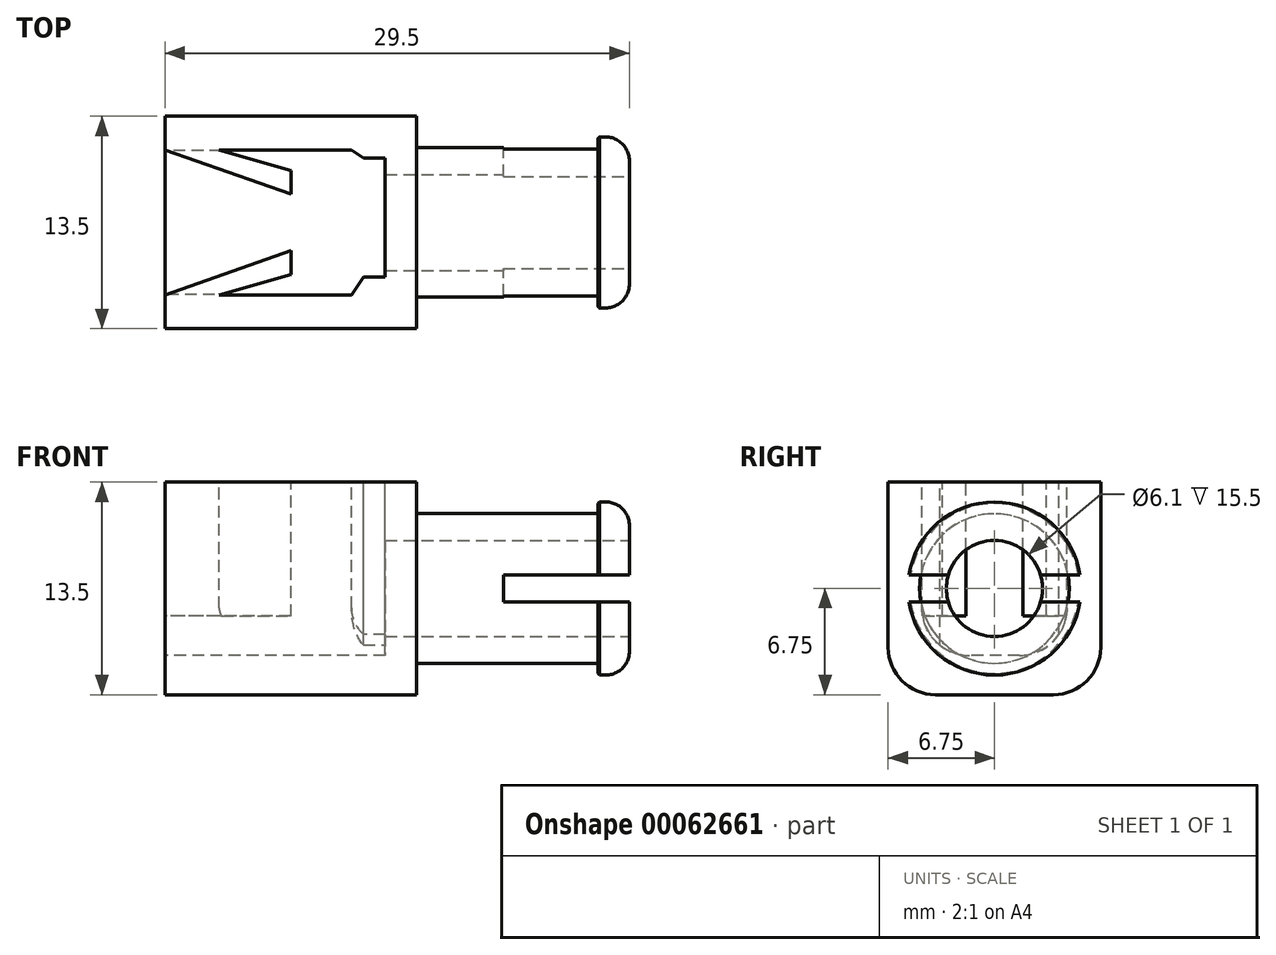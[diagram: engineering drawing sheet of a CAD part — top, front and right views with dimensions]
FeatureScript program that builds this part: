
annotation { "Feature Type Name" : "Feature", "Feature Type Description" : "" }
export const myFeature = defineFeature(function(context is Context, id is Id, definition is map)
    precondition{}
    {
        {
            var Q0;
            Q0=qCreatedBy(makeId("Top.planeOp"),FACE);
            var sketch = newSketch(context, id + "F0", { "sketchPlane" : qUnion([Q0])});
            skLineSegment(sketch, "E0.rect.bottom", {"start": v(-8, 6.75) * mm, "end": v(8, 6.75) * mm});
            skLineSegment(sketch, "E0.rect.top", {"start": v(-8, -6.75) * mm, "end": v(8, -6.75) * mm});
            skLineSegment(sketch, "E0.rect.left", {"start": v(-8, 6.75) * mm, "end": v(-8, -6.75) * mm});
            skLineSegment(sketch, "E0.rect.right", {"start": v(8, 6.75) * mm, "end": v(8, -6.75) * mm});
            skPoint(sketch, "E0.rect.middle", {"position": v(0, 0) * mm});
            skSolve(sketch);
        }
        {
            var Q0;
            Q0 = qSketchRegion(id + "F0", true);
            extrude(context, id + "F1", {"entities" : qUnion([Q0]), "depth" : 13.5 * mm});
        }
        {
            var Q0;
            Q0=makeQuery(id+"F1.opExtrude","SWEPT_FACE",FACE,{"disambiguationData":[OSD([sQuery(id+"F0.wireOp",EDGE,"E0.rect.right")])]});
            var sketch = newSketch(context, id + "F2", { "sketchPlane" : qUnion([Q0])});
            skCircle(sketch, "E1", {"center": v(0, 6.75) * mm, "radius": 4.75 * mm});
            skPoint(sketch, "E1.centerSnap0", {"position": v(-6.75, 6.75) * mm});
            skSolve(sketch);
        }
        {
            var Q0;
            Q0 = qSketchRegion(id + "F2", true);
            extrude(context, id + "F3", {"entities" : qUnion([Q0]), "operationType" : NewBodyOperationType.ADD, "depth" : 11.5 * mm});
        }
        {
            var Q0;
            Q0=makeQuery(id+"F3.opExtrude","CAP_FACE",FACE,{"disambiguationData":[OSD([sQuery(id+"F2.wireOp",EDGE,"E1")])],"isStart":false});
            var sketch = newSketch(context, id + "F4", { "sketchPlane" : qUnion([Q0])});
            skCircle(sketch, "E2", {"center": v(0, 6.75) * mm, "radius": 5.5 * mm});
            skSolve(sketch);
        }
        {
            var Q0;
            Q0 = qSketchRegion(id + "F4", true);
            extrude(context, id + "F5", {"entities" : qUnion([Q0]), "operationType" : NewBodyOperationType.ADD, "depth" : 2 * mm});
        }
        {
            var Q0;
            Q0=makeQuery(id+"F1.opExtrude","CAP_FACE",FACE,{"disambiguationData":[OSD([sQuery(id+"F0.wireOp",EDGE,"E0.rect.bottom"),sQuery(id+"F0.wireOp",EDGE,"E0.rect.top"),sQuery(id+"F0.wireOp",EDGE,"E0.rect.left"),sQuery(id+"F0.wireOp",EDGE,"E0.rect.right")])],"isStart":false});
            var sketch = newSketch(context, id + "F6", { "sketchPlane" : qUnion([Q0])});
            skLineSegment(sketch, "E3", {"start": v(0, 1.8) * mm, "end": v(0, 3.3) * mm});
            skLineSegment(sketch, "E4", {"start": v(0, 3.3) * mm, "end": v(-4.55, 4.6) * mm});
            skLineSegment(sketch, "E5", {"start": v(-4.55, 4.6) * mm, "end": v(3.85, 4.6) * mm});
            skLineSegment(sketch, "E6", {"start": v(3.85, 4.6) * mm, "end": v(4.6, 4.09) * mm});
            skLineSegment(sketch, "E7", {"start": v(4.6, 4.09) * mm, "end": v(6, 4.09) * mm});
            skLineSegment(sketch, "E8", {"start": v(6, 4.09) * mm, "end": v(6, -3.47) * mm});
            skLineSegment(sketch, "E9", {"start": v(6, -3.47) * mm, "end": v(4.6, -3.47) * mm});
            skLineSegment(sketch, "E10", {"start": v(4.6, -3.47) * mm, "end": v(3.85, -4.6) * mm});
            skLineSegment(sketch, "E11", {"start": v(3.85, -4.6) * mm, "end": v(-4.55, -4.6) * mm});
            skLineSegment(sketch, "E12", {"start": v(-4.55, -4.6) * mm, "end": v(0, -3.3) * mm});
            skLineSegment(sketch, "E13", {"start": v(0, -3.3) * mm, "end": v(0, -1.8) * mm});
            skLineSegment(sketch, "E14", {"start": v(0, -1.8) * mm, "end": v(-8, -4.6) * mm});
            skLineSegment(sketch, "E15", {"start": v(-8, 4.6) * mm, "end": v(0, 1.8) * mm});
            skSolve(sketch);
        }
        {
            var Q0;
            Q0=makeQuery(id+"F6.imprint","IMPRINT",FACE,{"disambiguationData":[TD([[makeQuery(id+"F6.imprint","IMPRINT",EDGE,{"derivedFrom":sQuery(id+"F6.wireOp",EDGE,"E3")}),-1.0]])]});
            extrude(context, id + "F7", {"entities" : qUnion([Q0]), "operationType" : NewBodyOperationType.REMOVE, "oppositeDirection" : true, "depth" : 11 * mm});
        }
        {
            var Q0;
            Q0=makeQuery(id+"F5.opExtrude","CAP_FACE",FACE,{"disambiguationData":[OSD([sQuery(id+"F4.wireOp",EDGE,"E2")])],"isStart":false});
            var sketch = newSketch(context, id + "F8", { "sketchPlane" : qUnion([Q0])});
            skCircle(sketch, "E16", {"center": v(0, 6.75) * mm, "radius": 3.05 * mm});
            skSolve(sketch);
        }
        {
            var Q0;
            Q0 = qSketchRegion(id + "F8", true);
            extrude(context, id + "F9", {"entities" : qUnion([Q0]), "operationType" : NewBodyOperationType.REMOVE, "oppositeDirection" : true, "depth" : 17 * mm});
        }
        {
            var Q0;
            Q0=makeQuery(id+"F1.opExtrude","SWEPT_FACE",FACE,{"disambiguationData":[OSD([sQuery(id+"F0.wireOp",EDGE,"E0.rect.left")])]});
            var sketch = newSketch(context, id + "F10", { "sketchPlane" : qUnion([Q0])});
            skLineSegment(sketch, "E17.bottom", {"start": v(-4.6, 2.5) * mm, "end": v(4.6, 2.5) * mm});
            skLineSegment(sketch, "E17.top", {"start": v(-4.6, 5) * mm, "end": v(4.6, 5) * mm});
            skLineSegment(sketch, "E17.left", {"start": v(-4.6, 2.5) * mm, "end": v(-4.6, 5) * mm});
            skLineSegment(sketch, "E17.right", {"start": v(4.6, 2.5) * mm, "end": v(4.6, 5) * mm});
            skSolve(sketch);
        }
        {
            var Q0;
            Q0 = qSketchRegion(id + "F10", true);
            extrude(context, id + "F11", {"entities" : qUnion([Q0]), "operationType" : NewBodyOperationType.REMOVE, "oppositeDirection" : true, "depth" : 10 * mm});
        }
        {
            var Q0;
            Q0=makeQuery(id+"F5.opExtrude","CAP_FACE",FACE,{"disambiguationData":[OSD([sQuery(id+"F4.wireOp",EDGE,"E2")])],"isStart":false});
            var sketch = newSketch(context, id + "F12", { "sketchPlane" : qUnion([Q0])});
            skLineSegment(sketch, "E18.rect.bottom", {"start": v(-6.07, 7.6) * mm, "end": v(6.07, 7.6) * mm});
            skLineSegment(sketch, "E18.rect.top", {"start": v(-6.07, 5.9) * mm, "end": v(6.07, 5.9) * mm});
            skLineSegment(sketch, "E18.rect.left", {"start": v(-6.07, 7.6) * mm, "end": v(-6.07, 5.9) * mm});
            skLineSegment(sketch, "E18.rect.right", {"start": v(6.07, 7.6) * mm, "end": v(6.07, 5.9) * mm});
            skPoint(sketch, "E18.rect.middle", {"position": v(0, 6.75) * mm});
            skSolve(sketch);
        }
        {
            var Q0;
            Q0 = qSketchRegion(id + "F12", true);
            extrude(context, id + "F13", {"entities" : qUnion([Q0]), "operationType" : NewBodyOperationType.REMOVE, "oppositeDirection" : true, "depth" : 8 * mm});
        }
        {
            var Q0;
            Q0=makeQuery(id+"F11.boolean.opBoolean","MERGE",EDGE,{"derivedFrom":[makeQuery(id+"F7.boolean.opBoolean","COPY",EDGE,{"derivedFrom":makeQuery(id+"F7.opExtrude","CAP_EDGE",EDGE,{"disambiguationData":[OSD([sQuery(id+"F6.wireOp",EDGE,"E5")])],"isStart":false})}),makeQuery(id+"F11.opExtrude","SWEPT_EDGE",EDGE,{"disambiguationData":[OSD([sQuery(id+"F10.wireOp",EDGE,"508b1908-c477-498a-9574-35cd2a2e4f79.bottom"),sQuery(id+"F10.wireOp",EDGE,"508b1908-c477-498a-9574-35cd2a2e4f79.left")])]})]});
            var Q1;
            Q1=makeQuery(id+"F11.boolean.opBoolean","MERGE",EDGE,{"derivedFrom":[makeQuery(id+"F7.boolean.opBoolean","COPY",EDGE,{"derivedFrom":makeQuery(id+"F7.opExtrude","CAP_EDGE",EDGE,{"disambiguationData":[OSD([sQuery(id+"F6.wireOp",EDGE,"E11")])],"isStart":false})}),makeQuery(id+"F11.opExtrude","SWEPT_EDGE",EDGE,{"disambiguationData":[OSD([sQuery(id+"F10.wireOp",EDGE,"508b1908-c477-498a-9574-35cd2a2e4f79.bottom"),sQuery(id+"F10.wireOp",EDGE,"508b1908-c477-498a-9574-35cd2a2e4f79.right")])]})]});
            var Q2;
            Q2=makeQuery(id+"F1.opExtrude","CAP_EDGE",EDGE,{"disambiguationData":[OSD([sQuery(id+"F0.wireOp",EDGE,"E0.rect.bottom")])],"isStart":true});
            var Q3;
            Q3=makeQuery(id+"F1.opExtrude","CAP_EDGE",EDGE,{"disambiguationData":[OSD([sQuery(id+"F0.wireOp",EDGE,"E0.rect.top")])],"isStart":true});
            var Q4;
            Q4=makeQuery(id+"F7.boolean.opBoolean","COPY",EDGE,{"derivedFrom":makeQuery(id+"F7.opExtrude","CAP_EDGE",EDGE,{"disambiguationData":[OSD([sQuery(id+"F6.wireOp",EDGE,"E11")])],"isStart":false})});
            fillet(context, id + "F14", {"entities" : qUnion([Q0, Q1, Q2, Q3, Q4]), "radius" : 3 * mm, "tangentPropagation" : true, "allowEdgeOverflow" : false});
        }
        {
            var Q0;
            {var subQ0=sQuery(id+"F4.wireOp",EDGE,"E2");Q0=makeQuery(id+"F13.boolean.opBoolean","SPLIT",EDGE,{"disambiguationData":[TD([makeQuery(id+"F13.opExtrude","SWEPT_FACE",FACE,{"disambiguationData":[OSD([sQuery(id+"F12.wireOp",EDGE,"E18.rect.bottom")])]})])],"derivedFrom":makeQuery(id+"F5.opExtrude","CAP_EDGE",EDGE,{"disambiguationData":[OSD([subQ0])],"isStart":false})});}
            var Q1;
            {var subQ0=sQuery(id+"F4.wireOp",EDGE,"E2");Q1=makeQuery(id+"F13.boolean.opBoolean","SPLIT",EDGE,{"disambiguationData":[TD([makeQuery(id+"F13.opExtrude","SWEPT_FACE",FACE,{"disambiguationData":[OSD([sQuery(id+"F12.wireOp",EDGE,"E18.rect.top")])]})])],"derivedFrom":makeQuery(id+"F5.opExtrude","CAP_EDGE",EDGE,{"disambiguationData":[OSD([subQ0])],"isStart":false})});}
            fillet(context, id + "F15", {"entities" : qUnion([Q0, Q1]), "radius" : 1.5 * mm, "tangentPropagation" : true, "allowEdgeOverflow" : false});
        }
        {
            var Q0;
            {var subQ0=sQuery(id+"F4.wireOp",EDGE,"E2");Q0=makeQuery(id+"F13.boolean.opBoolean","SPLIT",EDGE,{"disambiguationData":[TD([makeQuery(id+"F13.opExtrude","SWEPT_FACE",FACE,{"disambiguationData":[OSD([sQuery(id+"F12.wireOp",EDGE,"E18.rect.top")])]})])],"derivedFrom":makeQuery(id+"F5.opExtrude","CAP_EDGE",EDGE,{"disambiguationData":[OSD([subQ0])],"isStart":true})});}
            var Q1;
            {var subQ0=sQuery(id+"F4.wireOp",EDGE,"E2");Q1=makeQuery(id+"F13.boolean.opBoolean","SPLIT",EDGE,{"disambiguationData":[TD([makeQuery(id+"F13.opExtrude","SWEPT_FACE",FACE,{"disambiguationData":[OSD([sQuery(id+"F12.wireOp",EDGE,"E18.rect.bottom")])]})])],"derivedFrom":makeQuery(id+"F5.opExtrude","CAP_EDGE",EDGE,{"disambiguationData":[OSD([subQ0])],"isStart":true})});}
            chamfer(context, id + "F16", {"entities" : qUnion([Q0, Q1]), "width" : 0.1 * mm, "tangentPropagation" : true});
        }
    });
